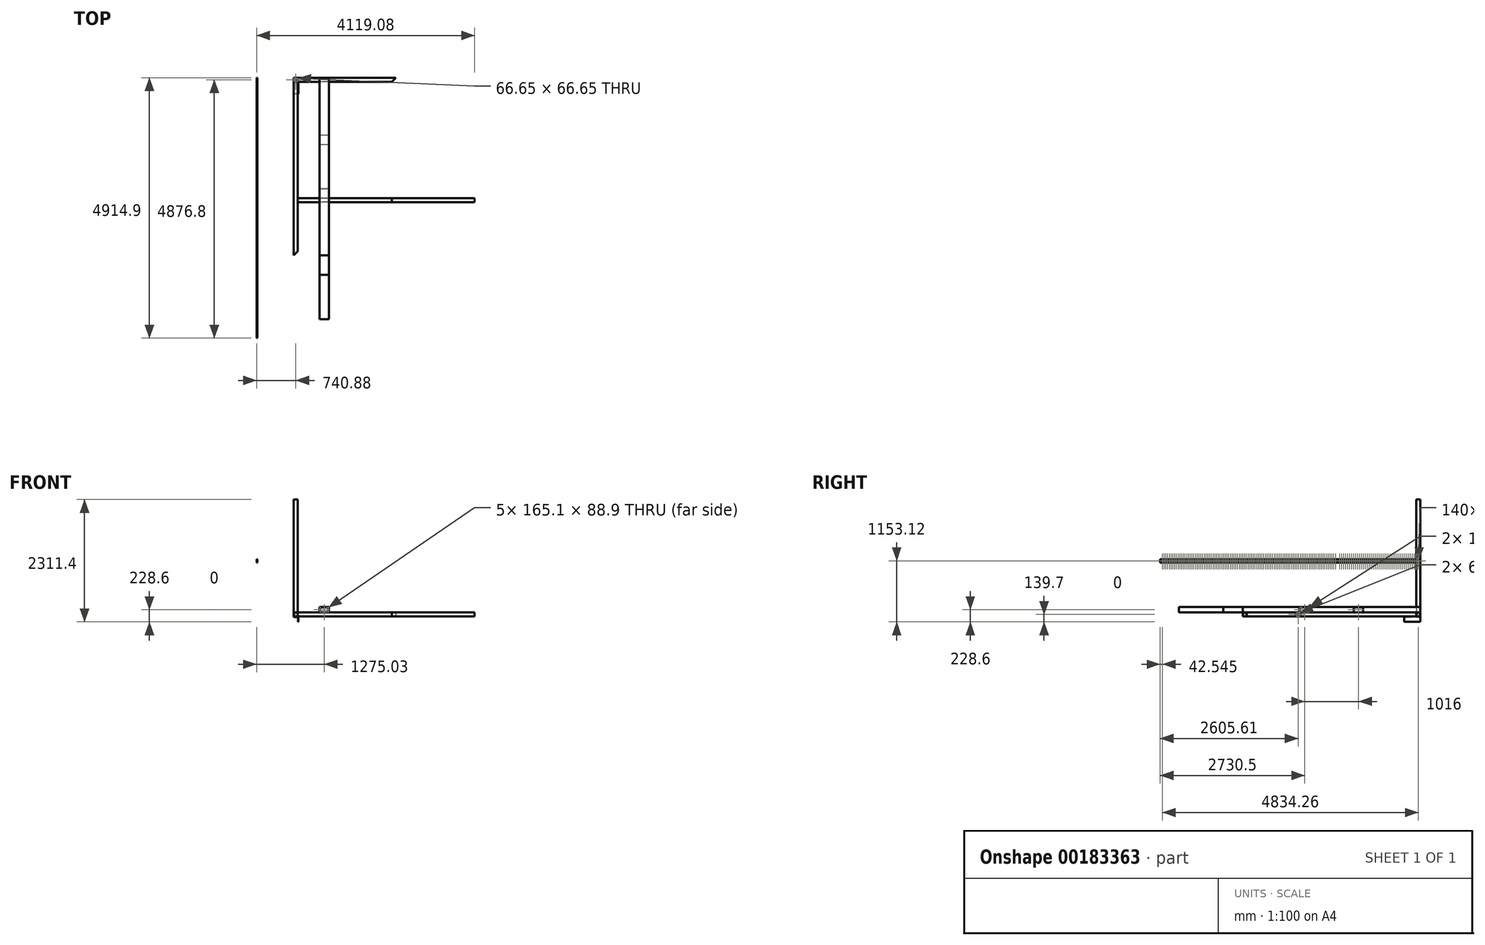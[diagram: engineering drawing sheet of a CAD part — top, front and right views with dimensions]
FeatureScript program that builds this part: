
annotation { "Feature Type Name" : "Feature", "Feature Type Description" : "" }
export const myFeature = defineFeature(function(context is Context, id is Id, definition is map)
    precondition{}
    {
        {
            var Q0;
            Q0=qCreatedBy(makeId("Front.planeOp"),FACE);
            var sketch = newSketch(context, id + "F0", { "sketchPlane" : qUnion([Q0])});
            skLineSegment(sketch, "E0.bottom", {"start": v(38.1, -38.1) * mm, "end": v(-38.1, -38.1) * mm});
            skLineSegment(sketch, "E0.top", {"start": v(38.1, 38.1) * mm, "end": v(-38.1, 38.1) * mm});
            skLineSegment(sketch, "E0.left", {"start": v(38.1, -38.1) * mm, "end": v(38.1, 38.1) * mm});
            skLineSegment(sketch, "E0.right", {"start": v(-38.1, -38.1) * mm, "end": v(-38.1, 38.1) * mm});
            skPoint(sketch, "E0.middle", {"position": v(0, 0) * mm});
            skLineSegment(sketch, "E1.0", {"start": v(33.32, 33.32) * mm, "end": v(-33.32, 33.32) * mm});
            skLineSegment(sketch, "E1.1", {"start": v(33.32, -33.32) * mm, "end": v(33.32, 33.32) * mm});
            skLineSegment(sketch, "E1.2", {"start": v(33.32, -33.32) * mm, "end": v(-33.32, -33.32) * mm});
            skLineSegment(sketch, "E1.3", {"start": v(-33.32, -33.32) * mm, "end": v(-33.32, 33.32) * mm});
            skSolve(sketch);
        }
        {
            var Q0;
            Q0 = qSketchRegion(id + "F0", true);
            extrude(context, id + "F1", {"entities" : qUnion([Q0]), "depth" : 3352.8 * mm});
        }
        {
            var Q0;
            Q0=makeQuery(id+"F1.opExtrude","SWEPT_FACE",FACE,{"disambiguationData":[OSD([sQuery(id+"F0.wireOp",EDGE,"E0.top")])]});
            var sketch = newSketch(context, id + "F2", { "sketchPlane" : qUnion([Q0])});
            skLineSegment(sketch, "E2", {"start": v(-38.1, 0) * mm, "end": v(38.1, -76.2) * mm});
            skSolve(sketch);
        }
        {
            var Q0;
            Q0 = qSketchRegion(id + "F2", true);
            var Q1;
            {var subQ0=sQuery(id+"F2.wireOp",EDGE,"E2");Q1=makeQuery(id+"F2.imprint","IMPRINT",FACE,{"disambiguationData":[TD([[makeQuery(id+"F2.imprint","IMPRINT",EDGE,{"derivedFrom":subQ0}),1.0]])]});}
            extrude(context, id + "F3", {"entities" : qUnion([Q0, Q1]), "operationType" : NewBodyOperationType.REMOVE, "endBound" : BoundingType.THROUGH_ALL, "oppositeDirection" : true, "depth" : 25.4 * mm});
        }
        {
            var Q0;
            Q0=makeQuery(id+"F1.opExtrude","SWEPT_FACE",FACE,{"disambiguationData":[OSD([sQuery(id+"F0.wireOp",EDGE,"E0.top")])]});
            var sketch = newSketch(context, id + "F4", { "sketchPlane" : qUnion([Q0])});
            skLineSegment(sketch, "E3", {"start": v(-38.1, -3352.8) * mm, "end": v(38.1, -3276.6) * mm});
            skSolve(sketch);
        }
        {
            var Q0;
            {var subQ0=sQuery(id+"F4.wireOp",EDGE,"E3");Q0=makeQuery(id+"F4.imprint","IMPRINT",FACE,{"disambiguationData":[TD([[makeQuery(id+"F4.imprint","IMPRINT",EDGE,{"derivedFrom":subQ0}),-1.0]])]});}
            extrude(context, id + "F5", {"entities" : qUnion([Q0]), "operationType" : NewBodyOperationType.REMOVE, "endBound" : BoundingType.THROUGH_ALL, "oppositeDirection" : true, "depth" : 25.4 * mm});
        }
        {
            var Q0;
            Q0=qCreatedBy(makeId("Right.planeOp"),FACE);
            cPlane(context, id + "F6", {"entities" : qUnion([Q0]), "cplaneType" : CPlaneType.OFFSET, "offset" : 38.1 * mm, "oppositeDirection" : true, "width" : 152.4 * mm, "height" : 152.4 * mm});
        }
        {
            var Q0;
            Q0=qCreatedBy(id+"F6.planeOp",FACE);
            var sketch = newSketch(context, id + "F7", { "sketchPlane" : qUnion([Q0])});
            skLineSegment(sketch, "E4.bottom", {"start": v(-76.2, -38.1) * mm, "end": v(0, -38.1) * mm});
            skLineSegment(sketch, "E4.top", {"start": v(-76.2, 38.1) * mm, "end": v(0, 38.1) * mm});
            skLineSegment(sketch, "E4.left", {"start": v(-76.2, -38.1) * mm, "end": v(-76.2, 38.1) * mm});
            skLineSegment(sketch, "E4.right", {"start": v(0, -38.1) * mm, "end": v(0, 38.1) * mm});
            skPoint(sketch, "E4.middle", {"position": v(0, 0) * mm});
            skLineSegment(sketch, "E5.0", {"start": v(-4.78, -33.32) * mm, "end": v(-4.78, 33.32) * mm});
            skLineSegment(sketch, "E5.1", {"start": v(-71.42, -33.32) * mm, "end": v(-4.78, -33.32) * mm});
            skLineSegment(sketch, "E5.2", {"start": v(-71.42, -33.32) * mm, "end": v(-71.42, 33.32) * mm});
            skLineSegment(sketch, "E5.3", {"start": v(-71.42, 33.32) * mm, "end": v(-4.78, 33.32) * mm});
            skSolve(sketch);
        }
        {
            var Q0;
            Q0=makeQuery(id+"F7.imprint","IMPRINT",FACE,{"disambiguationData":[TD([[makeQuery(id+"F7.imprint","IMPRINT",EDGE,{"derivedFrom":sQuery(id+"F7.wireOp",EDGE,"E4.bottom")}),1.0]])]});
            extrude(context, id + "F8", {"entities" : qUnion([Q0]), "depth" : 1930.4 * mm});
        }
        {
            var Q0;
            Q0=makeQuery(id+"F8.opExtrude","SWEPT_FACE",FACE,{"disambiguationData":[OSD([sQuery(id+"F7.wireOp",EDGE,"E4.top")])]});
            var sketch = newSketch(context, id + "F9", { "sketchPlane" : qUnion([Q0])});
            skLineSegment(sketch, "E6", {"start": v(-38.1, 0) * mm, "end": v(38.1, -76.2) * mm});
            skSolve(sketch);
        }
        {
            var Q0;
            {var subQ0=sQuery(id+"F9.wireOp",EDGE,"E6");Q0=makeQuery(id+"F9.imprint","IMPRINT",FACE,{"disambiguationData":[TD([[makeQuery(id+"F9.imprint","IMPRINT",EDGE,{"derivedFrom":subQ0}),-1.0]])]});}
            extrude(context, id + "F10", {"entities" : qUnion([Q0]), "operationType" : NewBodyOperationType.REMOVE, "endBound" : BoundingType.THROUGH_ALL, "oppositeDirection" : true, "depth" : 25.4 * mm});
        }
        {
            var Q0;
            Q0=makeQuery(id+"F8.opExtrude","SWEPT_FACE",FACE,{"disambiguationData":[OSD([sQuery(id+"F7.wireOp",EDGE,"E4.top")])]});
            var sketch = newSketch(context, id + "F11", { "sketchPlane" : qUnion([Q0])});
            skLineSegment(sketch, "E7", {"start": v(1892.3, 0) * mm, "end": v(1816.1, -76.2) * mm});
            skSolve(sketch);
        }
        {
            var Q0;
            Q0 = qSketchRegion(id + "F11", true);
            var Q1;
            {var subQ0=sQuery(id+"F11.wireOp",EDGE,"E7");Q1=makeQuery(id+"F11.imprint","IMPRINT",FACE,{"disambiguationData":[TD([[makeQuery(id+"F11.imprint","IMPRINT",EDGE,{"derivedFrom":subQ0}),1.0]])]});}
            extrude(context, id + "F12", {"entities" : qUnion([Q0, Q1]), "operationType" : NewBodyOperationType.REMOVE, "endBound" : BoundingType.THROUGH_ALL, "oppositeDirection" : true, "depth" : 25.4 * mm});
        }
        {
            var Q0;
            Q0=makeQuery(id+"F1.opExtrude","SWEPT_FACE",FACE,{"disambiguationData":[OSD([sQuery(id+"F0.wireOp",EDGE,"E0.top")])]});
            var sketch = newSketch(context, id + "F13", { "sketchPlane" : qUnion([Q0])});
            skLineSegment(sketch, "E8.bottom", {"start": v(-38.1, 0) * mm, "end": v(38.1, 0) * mm});
            skLineSegment(sketch, "E8.top", {"start": v(-38.1, -76.2) * mm, "end": v(38.1, -76.2) * mm});
            skLineSegment(sketch, "E8.left", {"start": v(-38.1, 0) * mm, "end": v(-38.1, -76.2) * mm});
            skLineSegment(sketch, "E8.right", {"start": v(38.1, 0) * mm, "end": v(38.1, -76.2) * mm});
            skLineSegment(sketch, "E9.0", {"start": v(-33.32, -4.78) * mm, "end": v(33.32, -4.78) * mm});
            skLineSegment(sketch, "E9.1", {"start": v(-33.32, -4.78) * mm, "end": v(-33.32, -71.42) * mm});
            skLineSegment(sketch, "E9.2", {"start": v(-33.32, -71.42) * mm, "end": v(33.32, -71.42) * mm});
            skLineSegment(sketch, "E9.3", {"start": v(33.32, -4.78) * mm, "end": v(33.32, -71.42) * mm});
            skSolve(sketch);
        }
        {
            var Q0;
            Q0 = qSketchRegion(id + "F13", true);
            extrude(context, id + "F14", {"entities" : qUnion([Q0]), "depth" : 2133.6 * mm});
        }
        {
            var Q0;
            Q0=makeQuery(id+"F8.opExtrude","SWEPT_FACE",FACE,{"disambiguationData":[OSD([sQuery(id+"F7.wireOp",EDGE,"E4.right")])]});
            var sketch = newSketch(context, id + "F15", { "sketchPlane" : qUnion([Q0])});
            skLineSegment(sketch, "E10", {"start": v(38.1, -38.1) * mm, "end": v(-50.8, -38.1) * mm});
            skLineSegment(sketch, "E11", {"start": v(-50.8, -38.1) * mm, "end": v(-50.8, -139.7) * mm});
            skLineSegment(sketch, "E12", {"start": v(-50.8, -139.7) * mm, "end": v(-41.27, -139.7) * mm});
            skLineSegment(sketch, "E13", {"start": v(-41.27, -139.7) * mm, "end": v(-41.27, -53.98) * mm});
            skLineSegment(sketch, "E14", {"start": v(-34.92, -47.63) * mm, "end": v(38.1, -47.62) * mm});
            skLineSegment(sketch, "E15", {"start": v(38.1, -47.63) * mm, "end": v(38.1, -38.1) * mm});
            skPoint(sketch, "E16.visualSharp", {"position": v(-41.27, -47.63) * mm});
            skArc(sketch, "E16.filletArc", {"start": v(-34.92, -47.62) * mm, "mid": v(-39.42, -49.48) * mm, "end": v(-41.28, -53.98) * mm});
            skSolve(sketch);
        }
        {
            var Q0;
            Q0=makeQuery(id+"F15.imprint","IMPRINT",FACE,{"disambiguationData":[TD([[makeQuery(id+"F15.imprint","IMPRINT",EDGE,{"derivedFrom":sQuery(id+"F15.wireOp",EDGE,"E10")}),-1.0]])]});
            extrude(context, id + "F16", {"entities" : qUnion([Q0]), "oppositeDirection" : true, "depth" : 304.8 * mm});
        }
        {
            var Q0;
            Q0=makeQuery(id+"F1.opExtrude","SWEPT_FACE",FACE,{"disambiguationData":[OSD([sQuery(id+"F0.wireOp",EDGE,"E0.left")])]});
            var sketch = newSketch(context, id + "F17", { "sketchPlane" : qUnion([Q0])});
            skLineSegment(sketch, "E17.bottom", {"start": v(-2347.39, 38.1) * mm, "end": v(-2271.19, 38.1) * mm});
            skLineSegment(sketch, "E17.top", {"start": v(-2347.39, -38.1) * mm, "end": v(-2271.19, -38.1) * mm});
            skLineSegment(sketch, "E17.left", {"start": v(-2347.39, 38.1) * mm, "end": v(-2347.39, -38.1) * mm});
            skLineSegment(sketch, "E17.right", {"start": v(-2271.19, 38.1) * mm, "end": v(-2271.19, -38.1) * mm});
            skLineSegment(sketch, "E18.0", {"start": v(-2275.96, 33.32) * mm, "end": v(-2275.96, -33.32) * mm});
            skLineSegment(sketch, "E18.1", {"start": v(-2342.61, 33.32) * mm, "end": v(-2275.96, 33.32) * mm});
            skLineSegment(sketch, "E18.2", {"start": v(-2342.61, 33.32) * mm, "end": v(-2342.61, -33.32) * mm});
            skLineSegment(sketch, "E18.3", {"start": v(-2342.61, -33.32) * mm, "end": v(-2275.96, -33.32) * mm});
            skSolve(sketch);
        }
        {
            var Q0;
            Q0 = qSketchRegion(id + "F17", true);
            extrude(context, id + "F18", {"entities" : qUnion([Q0]), "depth" : 1778 * mm});
        }
        {
            var Q0;
            Q0=makeQuery(id+"F8.opExtrude","SWEPT_FACE",FACE,{"disambiguationData":[OSD([sQuery(id+"F7.wireOp",EDGE,"E4.right")])]});
            var sketch = newSketch(context, id + "F19", { "sketchPlane" : qUnion([Q0])});
            skLineSegment(sketch, "E19", {"start": v(-445.25, 38.1) * mm, "end": v(-445.25, 139.7) * mm});
            skLineSegment(sketch, "E20", {"start": v(-445.25, 139.7) * mm, "end": v(-623.05, 139.7) * mm});
            skLineSegment(sketch, "E21", {"start": v(-623.05, 139.7) * mm, "end": v(-623.05, 38.1) * mm});
            skLineSegment(sketch, "E22", {"start": v(-623.05, 38.1) * mm, "end": v(-445.25, 38.1) * mm});
            skLineSegment(sketch, "E23.0", {"start": v(-616.7, 44.45) * mm, "end": v(-451.6, 44.45) * mm});
            skLineSegment(sketch, "E23.1", {"start": v(-616.7, 133.35) * mm, "end": v(-616.7, 44.45) * mm});
            skLineSegment(sketch, "E23.2", {"start": v(-451.6, 133.35) * mm, "end": v(-616.7, 133.35) * mm});
            skLineSegment(sketch, "E23.3", {"start": v(-451.6, 44.45) * mm, "end": v(-451.6, 133.35) * mm});
            skSolve(sketch);
        }
        {
            var Q0;
            Q0=makeQuery(id+"F19.imprint","IMPRINT",FACE,{"disambiguationData":[TD([[makeQuery(id+"F19.imprint","IMPRINT",EDGE,{"derivedFrom":sQuery(id+"F19.wireOp",EDGE,"E19")}),1.0]])]});
            extrude(context, id + "F20", {"entities" : qUnion([Q0]), "oppositeDirection" : true, "depth" : 3352.8 * mm});
        }
        {
            var Q0;
            Q0=makeQuery(id+"F20.opExtrude","CAP_FACE",FACE,{"disambiguationData":[OSD([sQuery(id+"F19.wireOp",EDGE,"E19"),sQuery(id+"F19.wireOp",EDGE,"E20"),sQuery(id+"F19.wireOp",EDGE,"E21"),sQuery(id+"F19.wireOp",EDGE,"E22"),sQuery(id+"F19.wireOp",EDGE,"E23.0"),sQuery(id+"F19.wireOp",EDGE,"E23.1"),sQuery(id+"F19.wireOp",EDGE,"E23.2"),sQuery(id+"F19.wireOp",EDGE,"E23.3")])],"isStart":false});
            extrude(context, id + "F21", {"entities" : qUnion([Q0]), "depth" : 368.3 * mm});
        }
        {
            var Q0;
            Q0=makeQuery(id+"F21.opExtrude","CAP_FACE",FACE,{"disambiguationData":[OSD([sQuery(id+"F19.wireOp",EDGE,"E19"),sQuery(id+"F19.wireOp",EDGE,"E20"),sQuery(id+"F19.wireOp",EDGE,"E21"),sQuery(id+"F19.wireOp",EDGE,"E22"),sQuery(id+"F19.wireOp",EDGE,"E23.0"),sQuery(id+"F19.wireOp",EDGE,"E23.1"),sQuery(id+"F19.wireOp",EDGE,"E23.2"),sQuery(id+"F19.wireOp",EDGE,"E23.3")])],"isStart":false});
            extrude(context, id + "F22", {"entities" : qUnion([Q0]), "depth" : 838.2 * mm});
        }
        {
            var Q0;
            Q0=makeQuery(id+"F20.opExtrude","SWEPT_FACE",FACE,{"disambiguationData":[OSD([sQuery(id+"F19.wireOp",EDGE,"E21")])]});
            var sketch = newSketch(context, id + "F23", { "sketchPlane" : qUnion([Q0])});
            skLineSegment(sketch, "E24", {"start": v(-1676.4, 139.7) * mm, "end": v(-1676.4, 38.1) * mm});
            skLineSegment(sketch, "E25.bottom", {"start": v(-2095.5, 42.88) * mm, "end": v(-2273.3, 42.88) * mm});
            skLineSegment(sketch, "E25.top", {"start": v(-2095.5, 134.92) * mm, "end": v(-2273.3, 134.92) * mm});
            skLineSegment(sketch, "E25.left", {"start": v(-2095.5, 42.88) * mm, "end": v(-2095.5, 134.92) * mm});
            skLineSegment(sketch, "E25.right", {"start": v(-2273.3, 42.88) * mm, "end": v(-2273.3, 134.92) * mm});
            skPoint(sketch, "E25.middle", {"position": v(-2184.4, 88.9) * mm});
            skLineSegment(sketch, "E26.bottom", {"start": v(-1079.5, 42.88) * mm, "end": v(-1257.3, 42.88) * mm});
            skLineSegment(sketch, "E26.top", {"start": v(-1079.5, 134.92) * mm, "end": v(-1257.3, 134.92) * mm});
            skLineSegment(sketch, "E26.left", {"start": v(-1079.5, 42.88) * mm, "end": v(-1079.5, 134.92) * mm});
            skLineSegment(sketch, "E26.right", {"start": v(-1257.3, 42.88) * mm, "end": v(-1257.3, 134.92) * mm});
            skPoint(sketch, "E26.middle", {"position": v(-1168.4, 88.9) * mm});
            skSolve(sketch);
        }
        {
            var Q0;
            {var subQ5=sQuery(id+"F23.wireOp",EDGE,"E25.right");Q0=makeQuery(id+"F23.imprint","IMPRINT",FACE,{"disambiguationData":[TD([[makeQuery(id+"F23.imprint","IMPRINT",EDGE,{"derivedFrom":subQ5}),-1.0]])]});}
            var Q1;
            {var subQ5=sQuery(id+"F23.wireOp",EDGE,"E25.left");Q1=makeQuery(id+"F23.imprint","IMPRINT",FACE,{"disambiguationData":[TD([[makeQuery(id+"F23.imprint","IMPRINT",EDGE,{"derivedFrom":subQ5}),1.0]])]});}
            var Q2;
            Q2=makeQuery(id+"F23.imprint","IMPRINT",FACE,{"disambiguationData":[TD([[makeQuery(id+"F23.imprint","IMPRINT",EDGE,{"derivedFrom":sQuery(id+"F23.wireOp",EDGE,"E26.bottom")}),-1.0]])]});
            extrude(context, id + "F24", {"entities" : qUnion([Q0, Q1, Q2]), "operationType" : NewBodyOperationType.REMOVE, "endBound" : BoundingType.THROUGH_ALL, "oppositeDirection" : true, "depth" : 25.4 * mm});
        }
        {
            var Q0;
            Q0=makeQuery(id+"F18.opExtrude","CAP_FACE",FACE,{"disambiguationData":[OSD([sQuery(id+"F17.wireOp",EDGE,"E17.bottom"),sQuery(id+"F17.wireOp",EDGE,"E17.top"),sQuery(id+"F17.wireOp",EDGE,"E17.left"),sQuery(id+"F17.wireOp",EDGE,"E17.right"),sQuery(id+"F17.wireOp",EDGE,"E18.0"),sQuery(id+"F17.wireOp",EDGE,"E18.1"),sQuery(id+"F17.wireOp",EDGE,"E18.2"),sQuery(id+"F17.wireOp",EDGE,"E18.3")])],"isStart":false});
            extrude(context, id + "F25", {"entities" : qUnion([Q0]), "depth" : 1562.1 * mm});
        }
        {
            var Q0;
            Q0=qCreatedBy(makeId("Front.planeOp"),FACE);
            var sketch = newSketch(context, id + "F26", { "sketchPlane" : qUnion([Q0])});
            skLineSegment(sketch, "E27", {"start": v(-740.88, 1045.18) * mm, "end": v(-728.18, 1045.18) * mm});
            skLineSegment(sketch, "E28", {"start": v(-728.18, 1045.18) * mm, "end": v(-728.18, 981.68) * mm});
            skLineSegment(sketch, "E29", {"start": v(-728.18, 981.68) * mm, "end": v(-740.88, 981.68) * mm});
            skLineSegment(sketch, "E30", {"start": v(-740.88, 981.68) * mm, "end": v(-740.88, 1045.18) * mm});
            skSolve(sketch);
        }
        {
            var Q0;
            Q0=makeQuery(id+"F26.imprint","IMPRINT",FACE,{"disambiguationData":[TD([[makeQuery(id+"F26.imprint","IMPRINT",EDGE,{"derivedFrom":sQuery(id+"F26.wireOp",EDGE,"E27")}),-1.0]])]});
            extrude(context, id + "F27", {"entities" : qUnion([Q0]), "depth" : 1562.1 * mm});
        }
        {
            var Q0;
            Q0=makeQuery(id+"F27.opExtrude","SWEPT_FACE",FACE,{"disambiguationData":[OSD([sQuery(id+"F26.wireOp",EDGE,"E30")])]});
            var sketch = newSketch(context, id + "F28", { "sketchPlane" : qUnion([Q0])});
            skCircle(sketch, "E31", {"center": v(38.1, 1013.43) * mm, "radius": 9.53 * mm});
            skPoint(sketch, "E31.centerSnap0", {"position": v(0, 1013.43) * mm});
            skCircle(sketch, "E32.1.0.0", {"center": v(76.2, 1013.43) * mm, "radius": 9.53 * mm});
            skCircle(sketch, "E32.2.0.0", {"center": v(114.3, 1013.43) * mm, "radius": 9.53 * mm});
            skCircle(sketch, "E32.3.0.0", {"center": v(152.4, 1013.43) * mm, "radius": 9.53 * mm});
            skCircle(sketch, "E32.4.0.0", {"center": v(190.5, 1013.43) * mm, "radius": 9.53 * mm});
            skCircle(sketch, "E32.5.0.0", {"center": v(228.6, 1013.43) * mm, "radius": 9.53 * mm});
            skCircle(sketch, "E32.6.0.0", {"center": v(266.7, 1013.43) * mm, "radius": 9.53 * mm});
            skCircle(sketch, "E32.7.0.0", {"center": v(304.8, 1013.43) * mm, "radius": 9.53 * mm});
            skCircle(sketch, "E32.8.0.0", {"center": v(342.9, 1013.43) * mm, "radius": 9.53 * mm});
            skCircle(sketch, "E32.9.0.0", {"center": v(381, 1013.43) * mm, "radius": 9.53 * mm});
            skCircle(sketch, "E32.10.0.0", {"center": v(419.1, 1013.43) * mm, "radius": 9.53 * mm});
            skCircle(sketch, "E32.11.0.0", {"center": v(457.2, 1013.43) * mm, "radius": 9.53 * mm});
            skCircle(sketch, "E32.12.0.0", {"center": v(495.3, 1013.43) * mm, "radius": 9.53 * mm});
            skCircle(sketch, "E32.13.0.0", {"center": v(533.4, 1013.43) * mm, "radius": 9.53 * mm});
            skCircle(sketch, "E32.14.0.0", {"center": v(571.5, 1013.43) * mm, "radius": 9.53 * mm});
            skCircle(sketch, "E32.15.0.0", {"center": v(609.6, 1013.43) * mm, "radius": 9.53 * mm});
            skCircle(sketch, "E32.16.0.0", {"center": v(647.7, 1013.43) * mm, "radius": 9.53 * mm});
            skCircle(sketch, "E32.17.0.0", {"center": v(685.8, 1013.43) * mm, "radius": 9.53 * mm});
            skCircle(sketch, "E32.18.0.0", {"center": v(723.9, 1013.43) * mm, "radius": 9.53 * mm});
            skCircle(sketch, "E32.19.0.0", {"center": v(762, 1013.43) * mm, "radius": 9.53 * mm});
            skCircle(sketch, "E32.20.0.0", {"center": v(800.1, 1013.43) * mm, "radius": 9.53 * mm});
            skCircle(sketch, "E32.21.0.0", {"center": v(838.2, 1013.43) * mm, "radius": 9.53 * mm});
            skCircle(sketch, "E32.22.0.0", {"center": v(876.3, 1013.43) * mm, "radius": 9.53 * mm});
            skCircle(sketch, "E32.23.0.0", {"center": v(914.4, 1013.43) * mm, "radius": 9.53 * mm});
            skCircle(sketch, "E32.24.0.0", {"center": v(952.5, 1013.43) * mm, "radius": 9.53 * mm});
            skCircle(sketch, "E32.25.0.0", {"center": v(990.6, 1013.43) * mm, "radius": 9.53 * mm});
            skCircle(sketch, "E32.26.0.0", {"center": v(1028.7, 1013.43) * mm, "radius": 9.53 * mm});
            skCircle(sketch, "E32.27.0.0", {"center": v(1066.8, 1013.43) * mm, "radius": 9.53 * mm});
            skCircle(sketch, "E32.28.0.0", {"center": v(1104.9, 1013.43) * mm, "radius": 9.53 * mm});
            skCircle(sketch, "E32.29.0.0", {"center": v(1143, 1013.43) * mm, "radius": 9.53 * mm});
            skCircle(sketch, "E32.30.0.0", {"center": v(1181.1, 1013.43) * mm, "radius": 9.53 * mm});
            skCircle(sketch, "E32.31.0.0", {"center": v(1219.2, 1013.43) * mm, "radius": 9.53 * mm});
            skCircle(sketch, "E32.32.0.0", {"center": v(1257.3, 1013.43) * mm, "radius": 9.53 * mm});
            skCircle(sketch, "E32.33.0.0", {"center": v(1295.4, 1013.43) * mm, "radius": 9.53 * mm});
            skCircle(sketch, "E32.34.0.0", {"center": v(1333.5, 1013.43) * mm, "radius": 9.53 * mm});
            skCircle(sketch, "E32.35.0.0", {"center": v(1371.6, 1013.43) * mm, "radius": 9.53 * mm});
            skCircle(sketch, "E32.36.0.0", {"center": v(1409.7, 1013.43) * mm, "radius": 9.53 * mm});
            skCircle(sketch, "E32.37.0.0", {"center": v(1447.8, 1013.43) * mm, "radius": 9.53 * mm});
            skCircle(sketch, "E32.38.0.0", {"center": v(1485.9, 1013.43) * mm, "radius": 9.53 * mm});
            skCircle(sketch, "E32.39.0.0", {"center": v(1524, 1013.43) * mm, "radius": 9.53 * mm});
            skLineSegment(sketch, "E32.direction1", {"start": v(38.1, 1013.43) * mm, "end": v(76.2, 1013.43) * mm, "construction": true});
            skSolve(sketch);
        }
        {
            var Q0;
            Q0 = qSketchRegion(id + "F28", true);
            extrude(context, id + "F29", {"entities" : qUnion([Q0]), "operationType" : NewBodyOperationType.REMOVE, "oppositeDirection" : true, "depth" : 25.4 * mm});
        }
        {
            var Q0;
            Q0=makeQuery(id+"F27.opExtrude","CAP_FACE",FACE,{"disambiguationData":[OSD([sQuery(id+"F26.wireOp",EDGE,"E27"),sQuery(id+"F26.wireOp",EDGE,"E28"),sQuery(id+"F26.wireOp",EDGE,"E29"),sQuery(id+"F26.wireOp",EDGE,"E30")])],"isStart":false});
            extrude(context, id + "F30", {"entities" : qUnion([Q0]), "depth" : 3352.8 * mm});
        }
        {
            var Q0;
            Q0=makeQuery(id+"F30.opExtrude","SWEPT_FACE",FACE,{"disambiguationData":[OSD([sQuery(id+"F26.wireOp",EDGE,"E30")])]});
            var sketch = newSketch(context, id + "F31", { "sketchPlane" : qUnion([Q0])});
            skCircle(sketch, "E33", {"center": v(1603.38, 1013.43) * mm, "radius": 9.53 * mm});
            skPoint(sketch, "E33.centerSnap0", {"position": v(1562.1, 1013.43) * mm});
            skCircle(sketch, "E34.1.0.0", {"center": v(1636.4, 1013.43) * mm, "radius": 9.53 * mm});
            skCircle(sketch, "E34.2.0.0", {"center": v(1669.42, 1013.43) * mm, "radius": 9.53 * mm});
            skCircle(sketch, "E34.3.0.0", {"center": v(1702.44, 1013.43) * mm, "radius": 9.53 * mm});
            skCircle(sketch, "E34.4.0.0", {"center": v(1735.46, 1013.43) * mm, "radius": 9.53 * mm});
            skCircle(sketch, "E34.5.0.0", {"center": v(1768.48, 1013.43) * mm, "radius": 9.53 * mm});
            skCircle(sketch, "E34.6.0.0", {"center": v(1801.5, 1013.43) * mm, "radius": 9.53 * mm});
            skCircle(sketch, "E34.7.0.0", {"center": v(1834.52, 1013.43) * mm, "radius": 9.53 * mm});
            skCircle(sketch, "E34.8.0.0", {"center": v(1867.54, 1013.43) * mm, "radius": 9.53 * mm});
            skCircle(sketch, "E34.9.0.0", {"center": v(1900.56, 1013.43) * mm, "radius": 9.53 * mm});
            skCircle(sketch, "E34.10.0.0", {"center": v(1933.58, 1013.43) * mm, "radius": 9.53 * mm});
            skCircle(sketch, "E34.11.0.0", {"center": v(1966.6, 1013.43) * mm, "radius": 9.53 * mm});
            skCircle(sketch, "E34.12.0.0", {"center": v(1999.62, 1013.43) * mm, "radius": 9.53 * mm});
            skCircle(sketch, "E34.13.0.0", {"center": v(2032.64, 1013.43) * mm, "radius": 9.53 * mm});
            skCircle(sketch, "E34.14.0.0", {"center": v(2065.66, 1013.43) * mm, "radius": 9.53 * mm});
            skCircle(sketch, "E34.15.0.0", {"center": v(2098.68, 1013.43) * mm, "radius": 9.53 * mm});
            skCircle(sketch, "E34.16.0.0", {"center": v(2131.7, 1013.43) * mm, "radius": 9.53 * mm});
            skCircle(sketch, "E34.17.0.0", {"center": v(2164.72, 1013.43) * mm, "radius": 9.53 * mm});
            skCircle(sketch, "E34.18.0.0", {"center": v(2197.74, 1013.43) * mm, "radius": 9.53 * mm});
            skCircle(sketch, "E34.19.0.0", {"center": v(2230.76, 1013.43) * mm, "radius": 9.53 * mm});
            skCircle(sketch, "E34.20.0.0", {"center": v(2263.78, 1013.43) * mm, "radius": 9.53 * mm});
            skCircle(sketch, "E34.21.0.0", {"center": v(2296.8, 1013.43) * mm, "radius": 9.53 * mm});
            skCircle(sketch, "E34.22.0.0", {"center": v(2329.82, 1013.43) * mm, "radius": 9.53 * mm});
            skCircle(sketch, "E34.23.0.0", {"center": v(2362.84, 1013.43) * mm, "radius": 9.53 * mm});
            skCircle(sketch, "E34.24.0.0", {"center": v(2395.86, 1013.43) * mm, "radius": 9.53 * mm});
            skCircle(sketch, "E34.25.0.0", {"center": v(2428.88, 1013.43) * mm, "radius": 9.53 * mm});
            skCircle(sketch, "E34.26.0.0", {"center": v(2461.9, 1013.43) * mm, "radius": 9.53 * mm});
            skCircle(sketch, "E34.27.0.0", {"center": v(2494.92, 1013.43) * mm, "radius": 9.53 * mm});
            skCircle(sketch, "E34.28.0.0", {"center": v(2527.94, 1013.43) * mm, "radius": 9.53 * mm});
            skCircle(sketch, "E34.29.0.0", {"center": v(2560.96, 1013.43) * mm, "radius": 9.53 * mm});
            skCircle(sketch, "E34.30.0.0", {"center": v(2593.98, 1013.43) * mm, "radius": 9.53 * mm});
            skCircle(sketch, "E34.31.0.0", {"center": v(2627, 1013.43) * mm, "radius": 9.53 * mm});
            skCircle(sketch, "E34.32.0.0", {"center": v(2660.02, 1013.43) * mm, "radius": 9.53 * mm});
            skCircle(sketch, "E34.33.0.0", {"center": v(2693.04, 1013.43) * mm, "radius": 9.53 * mm});
            skCircle(sketch, "E34.34.0.0", {"center": v(2726.06, 1013.43) * mm, "radius": 9.53 * mm});
            skCircle(sketch, "E34.35.0.0", {"center": v(2759.08, 1013.43) * mm, "radius": 9.53 * mm});
            skCircle(sketch, "E34.36.0.0", {"center": v(2792.1, 1013.43) * mm, "radius": 9.53 * mm});
            skCircle(sketch, "E34.37.0.0", {"center": v(2825.12, 1013.43) * mm, "radius": 9.53 * mm});
            skCircle(sketch, "E34.38.0.0", {"center": v(2858.14, 1013.43) * mm, "radius": 9.53 * mm});
            skCircle(sketch, "E34.39.0.0", {"center": v(2891.16, 1013.43) * mm, "radius": 9.53 * mm});
            skCircle(sketch, "E34.40.0.0", {"center": v(2924.18, 1013.43) * mm, "radius": 9.53 * mm});
            skCircle(sketch, "E34.41.0.0", {"center": v(2957.2, 1013.43) * mm, "radius": 9.53 * mm});
            skCircle(sketch, "E34.42.0.0", {"center": v(2990.22, 1013.43) * mm, "radius": 9.53 * mm});
            skCircle(sketch, "E34.43.0.0", {"center": v(3023.24, 1013.43) * mm, "radius": 9.53 * mm});
            skCircle(sketch, "E34.44.0.0", {"center": v(3056.26, 1013.43) * mm, "radius": 9.53 * mm});
            skCircle(sketch, "E34.45.0.0", {"center": v(3089.28, 1013.43) * mm, "radius": 9.53 * mm});
            skCircle(sketch, "E34.46.0.0", {"center": v(3122.3, 1013.43) * mm, "radius": 9.53 * mm});
            skCircle(sketch, "E34.47.0.0", {"center": v(3155.32, 1013.43) * mm, "radius": 9.53 * mm});
            skCircle(sketch, "E34.48.0.0", {"center": v(3188.34, 1013.43) * mm, "radius": 9.53 * mm});
            skCircle(sketch, "E34.49.0.0", {"center": v(3221.36, 1013.43) * mm, "radius": 9.53 * mm});
            skCircle(sketch, "E34.50.0.0", {"center": v(3254.38, 1013.43) * mm, "radius": 9.53 * mm});
            skCircle(sketch, "E34.51.0.0", {"center": v(3287.4, 1013.43) * mm, "radius": 9.53 * mm});
            skCircle(sketch, "E34.52.0.0", {"center": v(3320.42, 1013.43) * mm, "radius": 9.53 * mm});
            skCircle(sketch, "E34.53.0.0", {"center": v(3353.44, 1013.43) * mm, "radius": 9.53 * mm});
            skCircle(sketch, "E34.54.0.0", {"center": v(3386.46, 1013.43) * mm, "radius": 9.53 * mm});
            skCircle(sketch, "E34.55.0.0", {"center": v(3419.48, 1013.43) * mm, "radius": 9.53 * mm});
            skCircle(sketch, "E34.56.0.0", {"center": v(3452.5, 1013.43) * mm, "radius": 9.53 * mm});
            skCircle(sketch, "E34.57.0.0", {"center": v(3485.52, 1013.43) * mm, "radius": 9.53 * mm});
            skCircle(sketch, "E34.58.0.0", {"center": v(3518.54, 1013.43) * mm, "radius": 9.53 * mm});
            skCircle(sketch, "E34.59.0.0", {"center": v(3551.56, 1013.43) * mm, "radius": 9.53 * mm});
            skCircle(sketch, "E34.60.0.0", {"center": v(3584.58, 1013.43) * mm, "radius": 9.53 * mm});
            skCircle(sketch, "E34.61.0.0", {"center": v(3617.6, 1013.43) * mm, "radius": 9.53 * mm});
            skCircle(sketch, "E34.62.0.0", {"center": v(3650.62, 1013.43) * mm, "radius": 9.53 * mm});
            skCircle(sketch, "E34.63.0.0", {"center": v(3683.64, 1013.43) * mm, "radius": 9.53 * mm});
            skCircle(sketch, "E34.64.0.0", {"center": v(3716.66, 1013.43) * mm, "radius": 9.53 * mm});
            skCircle(sketch, "E34.65.0.0", {"center": v(3749.68, 1013.43) * mm, "radius": 9.53 * mm});
            skCircle(sketch, "E34.66.0.0", {"center": v(3782.7, 1013.43) * mm, "radius": 9.53 * mm});
            skCircle(sketch, "E34.67.0.0", {"center": v(3815.72, 1013.43) * mm, "radius": 9.53 * mm});
            skCircle(sketch, "E34.68.0.0", {"center": v(3848.74, 1013.43) * mm, "radius": 9.53 * mm});
            skCircle(sketch, "E34.69.0.0", {"center": v(3881.76, 1013.43) * mm, "radius": 9.53 * mm});
            skCircle(sketch, "E34.70.0.0", {"center": v(3914.78, 1013.43) * mm, "radius": 9.53 * mm});
            skCircle(sketch, "E34.71.0.0", {"center": v(3947.8, 1013.43) * mm, "radius": 9.53 * mm});
            skCircle(sketch, "E34.72.0.0", {"center": v(3980.82, 1013.43) * mm, "radius": 9.53 * mm});
            skCircle(sketch, "E34.73.0.0", {"center": v(4013.84, 1013.43) * mm, "radius": 9.53 * mm});
            skCircle(sketch, "E34.74.0.0", {"center": v(4046.86, 1013.43) * mm, "radius": 9.53 * mm});
            skCircle(sketch, "E34.75.0.0", {"center": v(4079.88, 1013.43) * mm, "radius": 9.53 * mm});
            skCircle(sketch, "E34.76.0.0", {"center": v(4112.9, 1013.43) * mm, "radius": 9.53 * mm});
            skCircle(sketch, "E34.77.0.0", {"center": v(4145.92, 1013.43) * mm, "radius": 9.53 * mm});
            skCircle(sketch, "E34.78.0.0", {"center": v(4178.94, 1013.43) * mm, "radius": 9.53 * mm});
            skCircle(sketch, "E34.79.0.0", {"center": v(4211.96, 1013.43) * mm, "radius": 9.53 * mm});
            skCircle(sketch, "E34.80.0.0", {"center": v(4244.98, 1013.43) * mm, "radius": 9.53 * mm});
            skCircle(sketch, "E34.81.0.0", {"center": v(4278, 1013.43) * mm, "radius": 9.53 * mm});
            skCircle(sketch, "E34.82.0.0", {"center": v(4311.02, 1013.43) * mm, "radius": 9.53 * mm});
            skCircle(sketch, "E34.83.0.0", {"center": v(4344.04, 1013.43) * mm, "radius": 9.53 * mm});
            skCircle(sketch, "E34.84.0.0", {"center": v(4377.06, 1013.43) * mm, "radius": 9.53 * mm});
            skCircle(sketch, "E34.85.0.0", {"center": v(4410.08, 1013.43) * mm, "radius": 9.53 * mm});
            skCircle(sketch, "E34.86.0.0", {"center": v(4443.1, 1013.43) * mm, "radius": 9.53 * mm});
            skCircle(sketch, "E34.87.0.0", {"center": v(4476.12, 1013.43) * mm, "radius": 9.53 * mm});
            skCircle(sketch, "E34.88.0.0", {"center": v(4509.14, 1013.43) * mm, "radius": 9.53 * mm});
            skCircle(sketch, "E34.89.0.0", {"center": v(4542.16, 1013.43) * mm, "radius": 9.53 * mm});
            skCircle(sketch, "E34.90.0.0", {"center": v(4575.18, 1013.43) * mm, "radius": 9.53 * mm});
            skCircle(sketch, "E34.91.0.0", {"center": v(4608.2, 1013.43) * mm, "radius": 9.53 * mm});
            skCircle(sketch, "E34.92.0.0", {"center": v(4641.22, 1013.43) * mm, "radius": 9.53 * mm});
            skCircle(sketch, "E34.93.0.0", {"center": v(4674.24, 1013.43) * mm, "radius": 9.53 * mm});
            skCircle(sketch, "E34.94.0.0", {"center": v(4707.26, 1013.43) * mm, "radius": 9.53 * mm});
            skCircle(sketch, "E34.95.0.0", {"center": v(4740.28, 1013.43) * mm, "radius": 9.53 * mm});
            skCircle(sketch, "E34.96.0.0", {"center": v(4773.3, 1013.43) * mm, "radius": 9.53 * mm});
            skCircle(sketch, "E34.97.0.0", {"center": v(4806.32, 1013.43) * mm, "radius": 9.53 * mm});
            skCircle(sketch, "E34.98.0.0", {"center": v(4839.34, 1013.43) * mm, "radius": 9.53 * mm});
            skCircle(sketch, "E34.99.0.0", {"center": v(4872.36, 1013.43) * mm, "radius": 9.53 * mm});
            skLineSegment(sketch, "E34.direction1", {"start": v(1603.38, 1013.43) * mm, "end": v(1636.4, 1013.43) * mm, "construction": true});
            skSolve(sketch);
        }
        {
            var Q0;
            Q0 = qSketchRegion(id + "F31", true);
            extrude(context, id + "F32", {"entities" : qUnion([Q0]), "operationType" : NewBodyOperationType.REMOVE, "oppositeDirection" : true, "depth" : 25.4 * mm});
        }
    });
